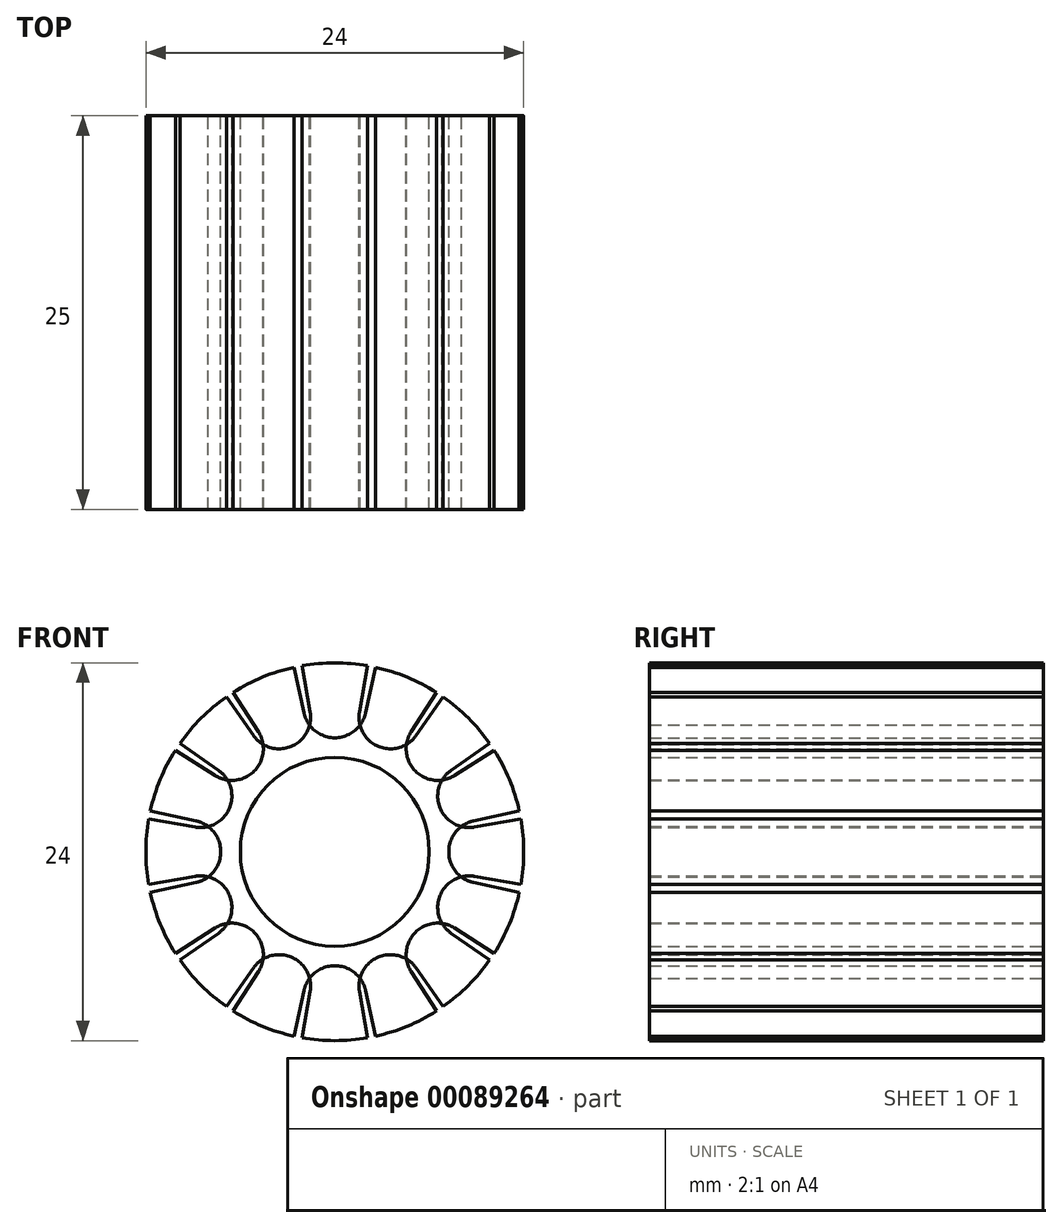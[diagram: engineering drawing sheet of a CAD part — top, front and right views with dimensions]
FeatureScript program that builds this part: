
annotation { "Feature Type Name" : "Feature", "Feature Type Description" : "" }
export const myFeature = defineFeature(function(context is Context, id is Id, definition is map)
    precondition{}
    {
        {
            var Q0;
            Q0=qCreatedBy(makeId("Front.planeOp"),FACE);
            var sketch = newSketch(context, id + "F0", { "sketchPlane" : qUnion([Q0])});
            skCircle(sketch, "E0", {"center": v(0, 0) * mm, "radius": 12 * mm});
            skCircle(sketch, "E1", {"center": v(0, 0) * mm, "radius": 6 * mm});
            skLineSegment(sketch, "E2", {"start": v(1.95, 8.8) * mm, "end": v(2.6, 11.72) * mm});
            skArc(sketch, "E3", {"start": v(-1.95, 8.8) * mm, "mid": v(0, 7.24) * mm, "end": v(1.95, 8.8) * mm});
            skLineSegment(sketch, "E4.trimOffspring", {"start": v(-1.95, 8.8) * mm, "end": v(-2.6, 11.72) * mm});
            skLineSegment(sketch, "E5.1.0", {"start": v(-5.17, 7.39) * mm, "end": v(-6.88, 9.83) * mm});
            skArc(sketch, "E5.1.1", {"start": v(-5.17, 7.39) * mm, "mid": v(-2.77, 6.69) * mm, "end": v(-1.57, 8.88) * mm});
            skLineSegment(sketch, "E5.1.2", {"start": v(-1.57, 8.88) * mm, "end": v(-2.08, 11.82) * mm});
            skLineSegment(sketch, "E5.2.0", {"start": v(-7.6, 4.85) * mm, "end": v(-10.12, 6.45) * mm});
            skArc(sketch, "E5.2.1", {"start": v(-7.6, 4.85) * mm, "mid": v(-5.12, 5.12) * mm, "end": v(-4.85, 7.6) * mm});
            skLineSegment(sketch, "E5.2.2", {"start": v(-4.85, 7.6) * mm, "end": v(-6.45, 10.12) * mm});
            skLineSegment(sketch, "E5.3.0", {"start": v(-8.88, 1.57) * mm, "end": v(-11.82, 2.08) * mm});
            skArc(sketch, "E5.3.1", {"start": v(-8.88, 1.57) * mm, "mid": v(-6.69, 2.77) * mm, "end": v(-7.39, 5.17) * mm});
            skLineSegment(sketch, "E5.3.2", {"start": v(-7.39, 5.17) * mm, "end": v(-9.83, 6.88) * mm});
            skLineSegment(sketch, "E5.4.0", {"start": v(-8.8, -1.95) * mm, "end": v(-11.72, -2.6) * mm});
            skArc(sketch, "E5.4.1", {"start": v(-8.8, -1.95) * mm, "mid": v(-7.24, 0) * mm, "end": v(-8.8, 1.95) * mm});
            skLineSegment(sketch, "E5.4.2", {"start": v(-8.8, 1.95) * mm, "end": v(-11.72, 2.6) * mm});
            skLineSegment(sketch, "E5.5.0", {"start": v(-7.39, -5.17) * mm, "end": v(-9.83, -6.88) * mm});
            skArc(sketch, "E5.5.1", {"start": v(-7.39, -5.17) * mm, "mid": v(-6.69, -2.77) * mm, "end": v(-8.88, -1.57) * mm});
            skLineSegment(sketch, "E5.5.2", {"start": v(-8.88, -1.57) * mm, "end": v(-11.82, -2.08) * mm});
            skLineSegment(sketch, "E5.6.0", {"start": v(-4.85, -7.6) * mm, "end": v(-6.45, -10.12) * mm});
            skArc(sketch, "E5.6.1", {"start": v(-4.85, -7.6) * mm, "mid": v(-5.12, -5.12) * mm, "end": v(-7.6, -4.85) * mm});
            skLineSegment(sketch, "E5.6.2", {"start": v(-7.6, -4.85) * mm, "end": v(-10.12, -6.45) * mm});
            skLineSegment(sketch, "E5.7.0", {"start": v(-1.57, -8.88) * mm, "end": v(-2.08, -11.82) * mm});
            skArc(sketch, "E5.7.1", {"start": v(-1.57, -8.88) * mm, "mid": v(-2.77, -6.69) * mm, "end": v(-5.17, -7.39) * mm});
            skLineSegment(sketch, "E5.7.2", {"start": v(-5.17, -7.39) * mm, "end": v(-6.88, -9.83) * mm});
            skLineSegment(sketch, "E5.8.0", {"start": v(1.95, -8.8) * mm, "end": v(2.6, -11.72) * mm});
            skArc(sketch, "E5.8.1", {"start": v(1.95, -8.8) * mm, "mid": v(0, -7.24) * mm, "end": v(-1.95, -8.8) * mm});
            skLineSegment(sketch, "E5.8.2", {"start": v(-1.95, -8.8) * mm, "end": v(-2.6, -11.72) * mm});
            skLineSegment(sketch, "E5.9.0", {"start": v(5.17, -7.39) * mm, "end": v(6.88, -9.83) * mm});
            skArc(sketch, "E5.9.1", {"start": v(5.17, -7.39) * mm, "mid": v(2.77, -6.69) * mm, "end": v(1.57, -8.88) * mm});
            skLineSegment(sketch, "E5.9.2", {"start": v(1.57, -8.88) * mm, "end": v(2.08, -11.82) * mm});
            skLineSegment(sketch, "E5.10.0", {"start": v(7.6, -4.85) * mm, "end": v(10.12, -6.45) * mm});
            skArc(sketch, "E5.10.1", {"start": v(7.6, -4.85) * mm, "mid": v(5.12, -5.12) * mm, "end": v(4.85, -7.6) * mm});
            skLineSegment(sketch, "E5.10.2", {"start": v(4.85, -7.6) * mm, "end": v(6.45, -10.12) * mm});
            skLineSegment(sketch, "E5.11.0", {"start": v(8.88, -1.57) * mm, "end": v(11.82, -2.08) * mm});
            skArc(sketch, "E5.11.1", {"start": v(8.88, -1.57) * mm, "mid": v(6.69, -2.77) * mm, "end": v(7.39, -5.17) * mm});
            skLineSegment(sketch, "E5.11.2", {"start": v(7.39, -5.17) * mm, "end": v(9.83, -6.88) * mm});
            skLineSegment(sketch, "E5.12.0", {"start": v(8.8, 1.95) * mm, "end": v(11.72, 2.6) * mm});
            skArc(sketch, "E5.12.1", {"start": v(8.8, 1.95) * mm, "mid": v(7.24, 0) * mm, "end": v(8.8, -1.95) * mm});
            skLineSegment(sketch, "E5.12.2", {"start": v(8.8, -1.95) * mm, "end": v(11.72, -2.6) * mm});
            skLineSegment(sketch, "E5.13.0", {"start": v(7.39, 5.17) * mm, "end": v(9.83, 6.88) * mm});
            skArc(sketch, "E5.13.1", {"start": v(7.39, 5.17) * mm, "mid": v(6.69, 2.77) * mm, "end": v(8.88, 1.57) * mm});
            skLineSegment(sketch, "E5.13.2", {"start": v(8.88, 1.57) * mm, "end": v(11.82, 2.08) * mm});
            skLineSegment(sketch, "E5.14.0", {"start": v(4.85, 7.6) * mm, "end": v(6.45, 10.12) * mm});
            skArc(sketch, "E5.14.1", {"start": v(4.85, 7.6) * mm, "mid": v(5.12, 5.12) * mm, "end": v(7.6, 4.85) * mm});
            skLineSegment(sketch, "E5.14.2", {"start": v(7.6, 4.85) * mm, "end": v(10.12, 6.45) * mm});
            skLineSegment(sketch, "E5.15.0", {"start": v(1.57, 8.88) * mm, "end": v(2.08, 11.82) * mm});
            skArc(sketch, "E5.15.1", {"start": v(1.57, 8.88) * mm, "mid": v(2.77, 6.69) * mm, "end": v(5.17, 7.39) * mm});
            skLineSegment(sketch, "E5.15.2", {"start": v(5.17, 7.39) * mm, "end": v(6.88, 9.83) * mm});
            skSolve(sketch);
        }
        {
            var Q0;
            {var subQ0=sQuery(id+"F0.wireOp",EDGE,"E4.trimOffspring");Q0=makeQuery(id+"F0.imprint","IMPRINT",FACE,{"disambiguationData":[TD([[makeQuery(id+"F0.imprint","IMPRINT",EDGE,{"derivedFrom":subQ0}),1.0]])]});}
            var Q1;
            {var subQ0=sQuery(id+"F0.wireOp",EDGE,"E5.1.2");Q1=makeQuery(id+"F0.imprint","IMPRINT",FACE,{"disambiguationData":[TD([[makeQuery(id+"F0.imprint","IMPRINT",EDGE,{"derivedFrom":subQ0}),-1.0]])]});}
            var Q2;
            {var subQ0=sQuery(id+"F0.wireOp",EDGE,"E2");Q2=makeQuery(id+"F0.imprint","IMPRINT",FACE,{"disambiguationData":[TD([[makeQuery(id+"F0.imprint","IMPRINT",EDGE,{"derivedFrom":subQ0}),-1.0]])]});}
            var Q3;
            {var subQ5=sQuery(id+"F0.wireOp",EDGE,"E5.13.0");Q3=makeQuery(id+"F0.imprint","IMPRINT",FACE,{"disambiguationData":[TD([[makeQuery(id+"F0.imprint","IMPRINT",EDGE,{"derivedFrom":subQ5}),1.0]])]});}
            var Q4;
            {var subQ1=sQuery(id+"F0.wireOp",EDGE,"E5.12.0");Q4=makeQuery(id+"F0.imprint","IMPRINT",FACE,{"disambiguationData":[TD([[makeQuery(id+"F0.imprint","IMPRINT",EDGE,{"derivedFrom":subQ1}),1.0]])]});}
            var Q5;
            {var subQ5=sQuery(id+"F0.wireOp",EDGE,"E5.11.0");Q5=makeQuery(id+"F0.imprint","IMPRINT",FACE,{"disambiguationData":[TD([[makeQuery(id+"F0.imprint","IMPRINT",EDGE,{"derivedFrom":subQ5}),1.0]])]});}
            var Q6;
            {var subQ5=sQuery(id+"F0.wireOp",EDGE,"E5.9.0");Q6=makeQuery(id+"F0.imprint","IMPRINT",FACE,{"disambiguationData":[TD([[makeQuery(id+"F0.imprint","IMPRINT",EDGE,{"derivedFrom":subQ5}),1.0]])]});}
            var Q7;
            {var subQ5=sQuery(id+"F0.wireOp",EDGE,"E5.7.0");Q7=makeQuery(id+"F0.imprint","IMPRINT",FACE,{"disambiguationData":[TD([[makeQuery(id+"F0.imprint","IMPRINT",EDGE,{"derivedFrom":subQ5}),1.0]])]});}
            var Q8;
            {var subQ5=sQuery(id+"F0.wireOp",EDGE,"E5.6.0");Q8=makeQuery(id+"F0.imprint","IMPRINT",FACE,{"disambiguationData":[TD([[makeQuery(id+"F0.imprint","IMPRINT",EDGE,{"derivedFrom":subQ5}),1.0]])]});}
            var Q9;
            {var subQ1=sQuery(id+"F0.wireOp",EDGE,"E5.5.0");Q9=makeQuery(id+"F0.imprint","IMPRINT",FACE,{"disambiguationData":[TD([[makeQuery(id+"F0.imprint","IMPRINT",EDGE,{"derivedFrom":subQ1}),1.0]])]});}
            var Q10;
            {var subQ5=sQuery(id+"F0.wireOp",EDGE,"E5.4.0");Q10=makeQuery(id+"F0.imprint","IMPRINT",FACE,{"disambiguationData":[TD([[makeQuery(id+"F0.imprint","IMPRINT",EDGE,{"derivedFrom":subQ5}),1.0]])]});}
            var Q11;
            {var subQ1=sQuery(id+"F0.wireOp",EDGE,"E5.3.0");Q11=makeQuery(id+"F0.imprint","IMPRINT",FACE,{"disambiguationData":[TD([[makeQuery(id+"F0.imprint","IMPRINT",EDGE,{"derivedFrom":subQ1}),1.0]])]});}
            var Q12;
            {var subQ6=sQuery(id+"F0.wireOp",EDGE,"E5.2.0");Q12=makeQuery(id+"F0.imprint","IMPRINT",FACE,{"disambiguationData":[TD([[makeQuery(id+"F0.imprint","IMPRINT",EDGE,{"derivedFrom":subQ6}),1.0]])]});}
            var Q13;
            {var subQ5=sQuery(id+"F0.wireOp",EDGE,"E5.1.0");Q13=makeQuery(id+"F0.imprint","IMPRINT",FACE,{"disambiguationData":[TD([[makeQuery(id+"F0.imprint","IMPRINT",EDGE,{"derivedFrom":subQ5}),1.0]])]});}
            var Q14;
            {var subQ5=sQuery(id+"F0.wireOp",EDGE,"E5.8.0");Q14=makeQuery(id+"F0.imprint","IMPRINT",FACE,{"disambiguationData":[TD([[makeQuery(id+"F0.imprint","IMPRINT",EDGE,{"derivedFrom":subQ5}),1.0]])]});}
            var Q15;
            {var subQ1=sQuery(id+"F0.wireOp",EDGE,"E5.10.0");Q15=makeQuery(id+"F0.imprint","IMPRINT",FACE,{"disambiguationData":[TD([[makeQuery(id+"F0.imprint","IMPRINT",EDGE,{"derivedFrom":subQ1}),1.0]])]});}
            var Q16;
            Q16=makeQuery(id+"F0.imprint","IMPRINT",FACE,{"disambiguationData":[TD([[makeQuery(id+"F0.imprint","IMPRINT",EDGE,{"derivedFrom":sQuery(id+"F0.wireOp",EDGE,"E1")}),1.0]])]});
            extrude(context, id + "F1", {"entities" : qUnion([Q0, Q1, Q2, Q3, Q4, Q5, Q6, Q7, Q8, Q9, Q10, Q11, Q12, Q13, Q14, Q15, Q16]), "depth" : 25 * mm});
        }
    });
